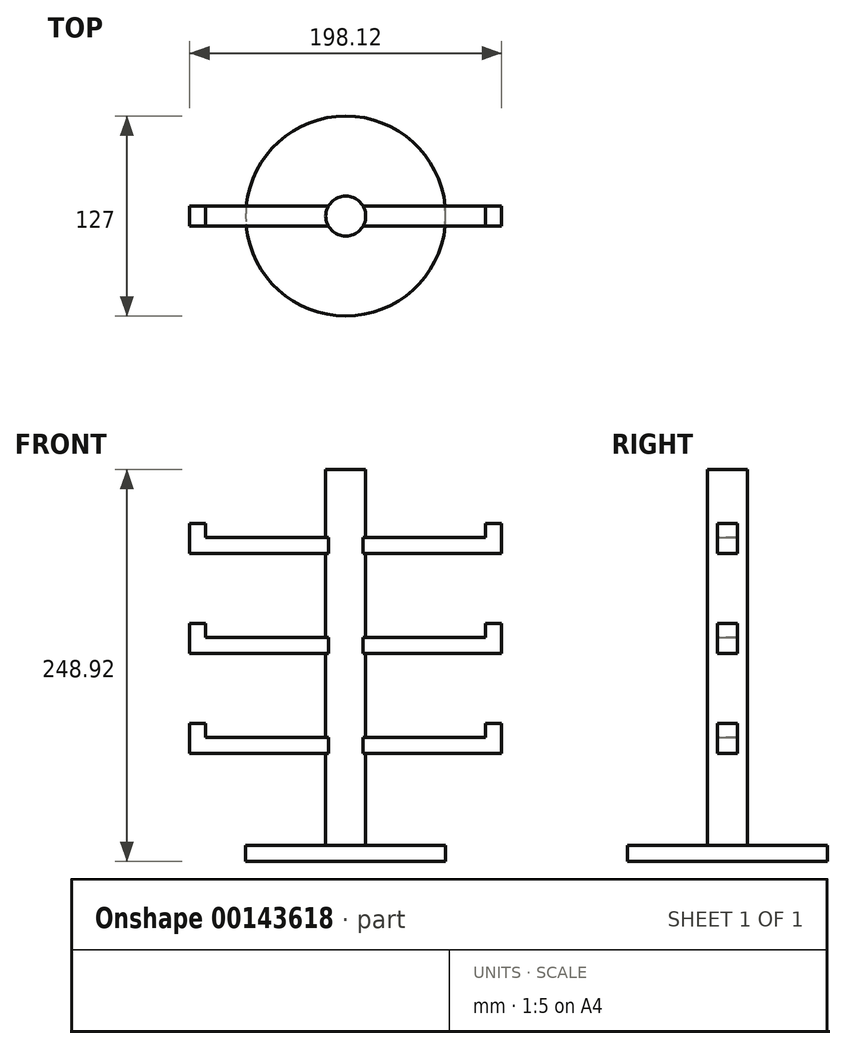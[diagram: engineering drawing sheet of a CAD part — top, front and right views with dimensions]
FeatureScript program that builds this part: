
annotation { "Feature Type Name" : "Feature", "Feature Type Description" : "" }
export const myFeature = defineFeature(function(context is Context, id is Id, definition is map)
    precondition{}
    {
        {
            var Q0;
            Q0=qCreatedBy(makeId("Top.planeOp"),FACE);
            var sketch = newSketch(context, id + "F0", { "sketchPlane" : qUnion([Q0])});
            skCircle(sketch, "E0", {"center": v(0, 0) * mm, "radius": 63.5 * mm});
            skSolve(sketch);
        }
        {
            var Q0;
            Q0 = qSketchRegion(id + "F0", true);
            extrude(context, id + "F1", {"entities" : qUnion([Q0]), "depth" : 10.16 * mm});
        }
        {
            var Q0;
            Q0=qCreatedBy(makeId("Top.planeOp"),FACE);
            var sketch = newSketch(context, id + "F2", { "sketchPlane" : qUnion([Q0])});
            skCircle(sketch, "E1", {"center": v(0, 0) * mm, "radius": 12.7 * mm});
            skSolve(sketch);
        }
        {
            var Q0;
            Q0 = qSketchRegion(id + "F2", true);
            extrude(context, id + "F3", {"entities" : qUnion([Q0]), "operationType" : NewBodyOperationType.ADD, "depth" : 248.92 * mm});
        }
        {
            var Q0;
            Q0=qCreatedBy(makeId("Front.planeOp"),FACE);
            var sketch = newSketch(context, id + "F4", { "sketchPlane" : qUnion([Q0])});
            skLineSegment(sketch, "E2.bottom", {"start": v(-88.9, 195.63) * mm, "end": v(88.9, 195.63) * mm});
            skLineSegment(sketch, "E2.top", {"start": v(-88.9, 205.79) * mm, "end": v(88.9, 205.79) * mm});
            skLineSegment(sketch, "E2.left", {"start": v(-88.9, 195.63) * mm, "end": v(-88.9, 205.79) * mm});
            skLineSegment(sketch, "E2.right", {"start": v(88.9, 195.63) * mm, "end": v(88.9, 205.79) * mm});
            skPoint(sketch, "E2.middle", {"position": v(0, 200.7) * mm});
            skLineSegment(sketch, "E3.bottom", {"start": v(-88.9, 142.29) * mm, "end": v(88.9, 142.29) * mm});
            skLineSegment(sketch, "E3.top", {"start": v(-88.9, 132.13) * mm, "end": v(88.9, 132.13) * mm});
            skLineSegment(sketch, "E3.left", {"start": v(-88.9, 142.29) * mm, "end": v(-88.9, 132.13) * mm});
            skLineSegment(sketch, "E3.right", {"start": v(88.9, 142.29) * mm, "end": v(88.9, 132.13) * mm});
            skPoint(sketch, "E3.middle", {"position": v(0, 137.2) * mm});
            skLineSegment(sketch, "E4.bottom", {"start": v(-88.9, 78.79) * mm, "end": v(88.9, 78.79) * mm});
            skLineSegment(sketch, "E4.top", {"start": v(-88.9, 68.63) * mm, "end": v(88.9, 68.63) * mm});
            skLineSegment(sketch, "E4.left", {"start": v(-88.9, 78.79) * mm, "end": v(-88.9, 68.63) * mm});
            skLineSegment(sketch, "E4.right", {"start": v(88.9, 78.79) * mm, "end": v(88.9, 68.63) * mm});
            skPoint(sketch, "E4.middle", {"position": v(0, 73.7) * mm});
            skLineSegment(sketch, "E5.bottom", {"start": v(-88.9, 68.63) * mm, "end": v(-99.06, 68.63) * mm});
            skLineSegment(sketch, "E5.top", {"start": v(-88.9, 87.68) * mm, "end": v(-99.06, 87.68) * mm});
            skLineSegment(sketch, "E5.left", {"start": v(-88.9, 68.63) * mm, "end": v(-88.9, 87.68) * mm});
            skLineSegment(sketch, "E5.right", {"start": v(-99.06, 68.63) * mm, "end": v(-99.06, 87.68) * mm});
            skLineSegment(sketch, "E6.bottom", {"start": v(-88.9, 132.13) * mm, "end": v(-99.06, 132.13) * mm});
            skLineSegment(sketch, "E6.top", {"start": v(-88.9, 151.18) * mm, "end": v(-99.06, 151.18) * mm});
            skLineSegment(sketch, "E6.left", {"start": v(-88.9, 132.13) * mm, "end": v(-88.9, 151.18) * mm});
            skLineSegment(sketch, "E6.right", {"start": v(-99.06, 132.13) * mm, "end": v(-99.06, 151.18) * mm});
            skLineSegment(sketch, "E7.bottom", {"start": v(-88.9, 195.63) * mm, "end": v(-99.06, 195.63) * mm});
            skLineSegment(sketch, "E7.top", {"start": v(-88.9, 214.68) * mm, "end": v(-99.06, 214.68) * mm});
            skLineSegment(sketch, "E7.left", {"start": v(-88.9, 195.63) * mm, "end": v(-88.9, 214.68) * mm});
            skLineSegment(sketch, "E7.right", {"start": v(-99.06, 195.63) * mm, "end": v(-99.06, 214.68) * mm});
            skLineSegment(sketch, "E8.bottom", {"start": v(88.9, 132.13) * mm, "end": v(99.06, 132.13) * mm});
            skLineSegment(sketch, "E8.top", {"start": v(88.9, 151.18) * mm, "end": v(99.06, 151.18) * mm});
            skLineSegment(sketch, "E8.left", {"start": v(88.9, 132.13) * mm, "end": v(88.9, 151.18) * mm});
            skLineSegment(sketch, "E8.right", {"start": v(99.06, 132.13) * mm, "end": v(99.06, 151.18) * mm});
            skLineSegment(sketch, "E9.bottom", {"start": v(88.9, 195.63) * mm, "end": v(99.06, 195.63) * mm});
            skLineSegment(sketch, "E9.top", {"start": v(88.9, 214.68) * mm, "end": v(99.06, 214.68) * mm});
            skLineSegment(sketch, "E9.left", {"start": v(88.9, 195.63) * mm, "end": v(88.9, 214.68) * mm});
            skLineSegment(sketch, "E9.right", {"start": v(99.06, 195.63) * mm, "end": v(99.06, 214.68) * mm});
            skLineSegment(sketch, "E10.bottom", {"start": v(88.9, 68.63) * mm, "end": v(99.06, 68.63) * mm});
            skLineSegment(sketch, "E10.top", {"start": v(88.9, 87.68) * mm, "end": v(99.06, 87.68) * mm});
            skLineSegment(sketch, "E10.left", {"start": v(88.9, 68.63) * mm, "end": v(88.9, 87.68) * mm});
            skLineSegment(sketch, "E10.right", {"start": v(99.06, 68.63) * mm, "end": v(99.06, 87.68) * mm});
            skLineSegment(sketch, "E11", {"start": v(0, 0) * mm, "end": v(0, 10.2) * mm});
            skLineSegment(sketch, "E12", {"start": v(0, 10.2) * mm, "end": v(0, 73.7) * mm});
            skLineSegment(sketch, "E13", {"start": v(0, 73.7) * mm, "end": v(0, 137.2) * mm});
            skLineSegment(sketch, "E14", {"start": v(0, 137.2) * mm, "end": v(0, 200.7) * mm});
            skSolve(sketch);
        }
        {
            var Q0;
            Q0 = qSketchRegion(id + "F4", true);
            extrude(context, id + "F5", {"entities" : qUnion([Q0]), "operationType" : NewBodyOperationType.ADD, "endBound" : BoundingType.SYMMETRIC, "depth" : 12.7 * mm});
        }
    });
